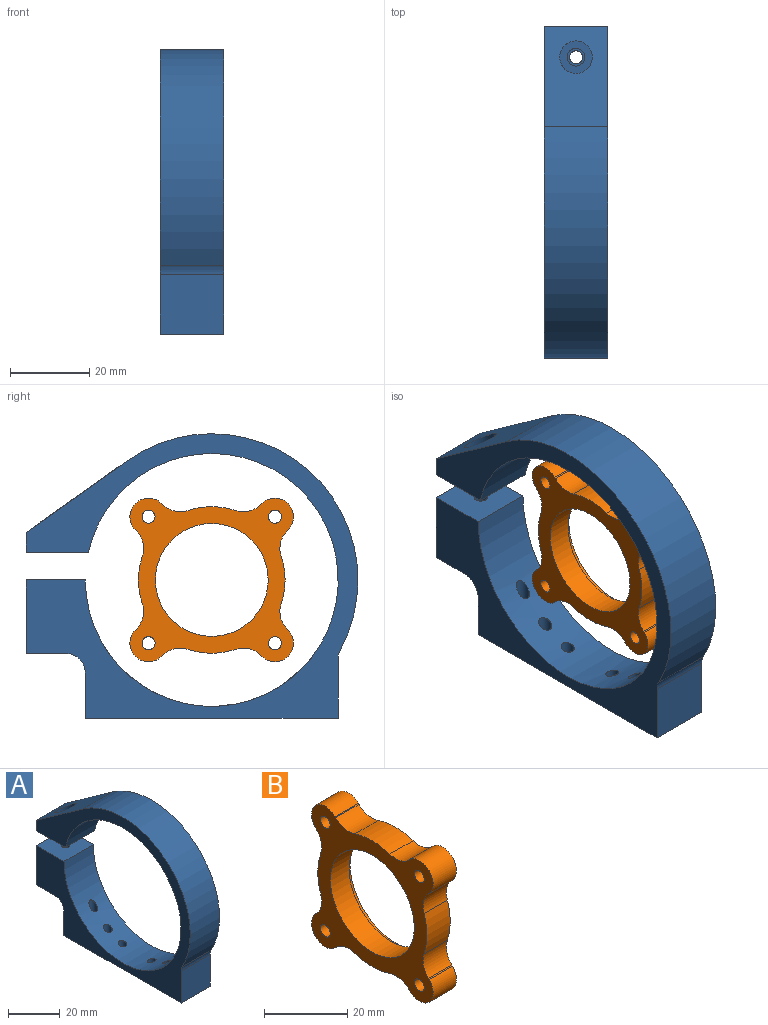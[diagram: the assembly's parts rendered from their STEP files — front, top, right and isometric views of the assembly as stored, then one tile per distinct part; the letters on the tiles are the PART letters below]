
ASSEMBLY  parts=2 mates=1
PART A: 25 faces, bbox 17.2x85.2x73.2 mm
  f0: cylinder r=32mm len=64.01mm, axis (-1,0,0), area 3041.4mm2, adj f1,f10,f11,f12,f13,f14,f15,f16
  f1: plane 16x15mm, normal (0,0,1), area 231.5mm2, adj f0,f2,f11,f12,f24
  f2: plane 18.58x16mm, normal (0,1,0), area 297.3mm2, adj f1,f3,f11,f12
  f3: plane 16x10mm, normal (0,0,-1), area 151.5mm2, adj f2,f11,f12,f19,f24
  f4: plane 16x11.42mm, normal (0,1,0), area 182.7mm2, adj f5,f11,f12,f19
  f5: plane 64x16mm, normal (0,0,-1), area 972.7mm2, adj f4,f6,f11,f12,f13,f14,f15,f16
  f6: plane 16x15.12mm, normal (0,-1,0), area 241.9mm2, adj f5,f11,f12,f20
  f7: cylinder r=37mm len=58.43mm, axis (-1,0,0), area 1587.6mm2, adj f8,f11,f12,f20
  f8: plane 26.81x19.4mm, normal (0,0.58,0.82), area 436.4mm2, adj f7,f9,f11,f12,f21
  f9: plane 16x5mm, normal (0,1,0), area 80mm2, adj f8,f10,f11,f12
  f10: plane 16x15.78mm, normal (0,0,-1), area 236.5mm2, adj f0,f9,f11,f12,f22
  f11: plane 84.01x72mm, normal (1,0,0), area 1623.4mm2, adj f0,f1,f2,f3,f4,f5,f6,f7
  f12: plane 84.01x72mm, normal (-1,0,0), area 1623.4mm2, adj f0,f1,f2,f3,f4,f5,f6,f7
  f13: cylinder r=1.65mm len=15.86mm, axis (0,0,-1), area 144.1mm2, adj f0,f5
  f14: cylinder r=1.65mm len=8.3mm, axis (0,0,-1), area 75.8mm2, adj f0,f5
  f15: cylinder r=1.65mm len=4.01mm, axis (0,0,-1), area 41.6mm2, adj f0,f5
  f16: cylinder r=1.65mm len=4.01mm, axis (0,0,-1), area 41.6mm2, adj f0,f5
  f17: cylinder r=1.65mm len=8.3mm, axis (0,0,-1), area 75.8mm2, adj f0,f5
  f18: cylinder r=1.65mm len=15.86mm, axis (0,0,-1), area 144.1mm2, adj f0,f5
  f19: cylinder r=5mm len=16mm, axis (1,0,0), area 125.7mm2, adj f3,f4,f11,f12
  f20: cylinder r=5mm len=16mm, axis (-1,0,0), area 39.4mm2, adj f6,f7,f11,f12
  f21: cylinder r=4.12mm len=8.53mm, axis (0,0,1), area 142.6mm2, adj f8,f23
  f22: cylinder r=2.25mm len=5mm, axis (0,0,1), area 70.7mm2, adj f10,f23
  f23: plane 8.25x8.25mm, normal (0,0,1), area 37.6mm2, adj f21,f22
  f24: cylinder r=1.65mm len=18.58mm, axis (0,0,1), area 192.6mm2, adj f1,f3
PART B: 33 faces, bbox 7.9x41.4x41.4 mm
  f0: cylinder r=4.7mm len=8.03mm, axis (1,0,0), area 117.3mm2, adj f1,f15,f17,f19
  f1: plane 7.94x0.22mm, normal (0,0.71,0.71), area 2.4mm2, adj f0,f17,f19,f25
  f2: cylinder r=18.56mm len=11.87mm, axis (1,0,0), area 95.9mm2, adj f17,f19,f25,f26
  f3: plane 7.94x0.22mm, normal (0,-0.71,0.71), area 2.4mm2, adj f4,f17,f19,f26
  f4: cylinder r=4.7mm len=8.03mm, axis (1,0,0), area 117.3mm2, adj f3,f5,f17,f19
  f5: plane 7.94x0.22mm, normal (0,0.71,-0.71), area 2.4mm2, adj f4,f17,f19,f27
  f6: cylinder r=18.56mm len=11.87mm, axis (1,0,0), area 95.9mm2, adj f17,f19,f27,f28
  f7: plane 7.94x0.22mm, normal (0,0.71,0.71), area 2.4mm2, adj f8,f17,f19,f28
  f8: cylinder r=4.7mm len=8.03mm, axis (1,0,0), area 117.3mm2, adj f7,f9,f17,f19
  f9: plane 7.94x0.22mm, normal (0,-0.71,-0.71), area 2.4mm2, adj f8,f17,f19,f29
  f10: cylinder r=18.56mm len=11.87mm, axis (1,0,0), area 95.9mm2, adj f17,f19,f29,f30
  f11: plane 7.94x0.22mm, normal (0,0.71,-0.71), area 2.4mm2, adj f12,f17,f19,f30
  f12: cylinder r=4.7mm len=8.03mm, axis (1,0,0), area 117.3mm2, adj f11,f13,f17,f19
  f13: plane 7.94x0.22mm, normal (0,-0.71,0.71), area 2.4mm2, adj f12,f17,f19,f31
  f14: cylinder r=18.56mm len=11.87mm, axis (1,0,0), area 95.9mm2, adj f17,f19,f31,f32
  f15: plane 7.94x0.22mm, normal (0,-0.71,-0.71), area 2.4mm2, adj f0,f17,f19,f32
  f16: cylinder r=15.56mm len=31.12mm, axis (1,0,0), area 155.2mm2, adj f17,f18
  f17: plane 41.41x41.41mm, normal (1,0,0), area 612.1mm2, adj f0,f1,f2,f3,f4,f5,f6,f7
  f18: plane 31.12x31.12mm, normal (1,0,0), area 120.2mm2, adj f16,f20
  f19: plane 41.41x41.41mm, normal (-1,0,0), area 732.3mm2, adj f0,f1,f2,f3,f4,f5,f6,f7
  f20: cylinder r=14.27mm len=28.55mm, axis (1,0,0), area 569.5mm2, adj f18,f19
  f21: cylinder r=1.65mm len=7.94mm, axis (-1,0,0), area 82.3mm2, adj f17,f19
  f22: cylinder r=1.65mm len=7.94mm, axis (-1,0,0), area 82.3mm2, adj f17,f19
  f23: cylinder r=1.65mm len=7.94mm, axis (-1,0,0), area 82.3mm2, adj f17,f19
  f24: cylinder r=1.65mm len=7.94mm, axis (-1,0,0), area 82.3mm2, adj f17,f19
  f25: cylinder r=6.35mm len=7.94mm, axis (1,0,0), area 56mm2, adj f1,f2,f17,f19
  f26: cylinder r=6.35mm len=7.94mm, axis (1,0,0), area 56mm2, adj f2,f3,f17,f19
  f27: cylinder r=6.35mm len=7.94mm, axis (1,0,0), area 56mm2, adj f5,f6,f17,f19
  f28: cylinder r=6.35mm len=7.94mm, axis (1,0,0), area 56mm2, adj f6,f7,f17,f19
  f29: cylinder r=6.35mm len=7.94mm, axis (1,0,0), area 56mm2, adj f9,f10,f17,f19
  f30: cylinder r=6.35mm len=7.94mm, axis (1,0,0), area 56mm2, adj f10,f11,f17,f19
  f31: cylinder r=6.35mm len=7.94mm, axis (1,0,0), area 56mm2, adj f13,f14,f17,f19
  f32: cylinder r=6.35mm len=7.94mm, axis (1,0,0), area 56mm2, adj f14,f15,f17,f19
PLACE A t=(-11.9,-27.3,14.3)mm
PLACE B t=(4.1,-27.3,73.3)mm
MATE fastened B.f20 <-> A.f0  axis (1,0,0) through (-14.73,-20.58,-4.02)mm
